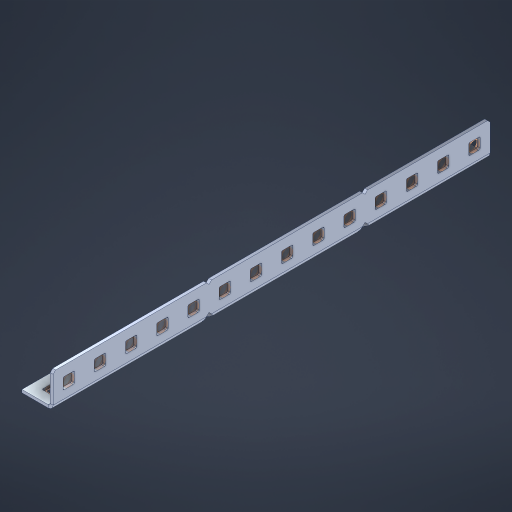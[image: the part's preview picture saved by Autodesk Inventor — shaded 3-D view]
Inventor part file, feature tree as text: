
AUTODESK INVENTOR PART (.ipt)
format: ipt  version: 2023 (Build 270158000, 158)  size: 627,712 bytes
history: native  units: in
note: dims shown in document units (in); Inventor stores cm internally (conversion verified against a paired STEP export)
features: other x33, extrude x27, sheet_metal_op x10, sketch x8, mirror x1, pattern_linear x1, chamfer x1
ambient origin geometry x8: Origin, YZ Plane, XZ Plane, XY Plane, X Axis, Y Axis, Z Axis, Center Point
bodies: Solid1 (feature_tree), Body (feature_tree)
feature tree (81):
  other  "Flange Pattern Plane"
  sheet_metal_op  "Flange Pattern"
  sheet_metal_op  "Body Pattern"
  other  "Arc Length"
  mirror  "Notch Mirror"
  pattern_linear  "Notch Pattern"  Spacing1=0.1875in  [1 undecoded]
  chamfer  "End Chamfer"
  extrude  "Half Cut"  Depth=0.0469in
  sketch  "Sketch1"  dims[d0=2.5in]
  other  "Plate1"
  sketch  "Sketch2"  dims[d1=7.0in]
  other  "Plate2"
  sheet_metal_op  "Bend1"
  sheet_metal_op  "Corner1"
  sketch  "Sketch3"  dims[d2=0.0469in]
  other  "Flange Pattern Sketch"
  sketch  "Sketch7"  dims[d3=0.0469in]
  other  "Srf1"
  other  "Srf2"
  sketch  "Sketch8"  dims[d4=0.0234in]
  sketch  "Sketch9"  dims[d5=0.0938in]
  other  "Srf91"
  sheet_metal_op  "Body Pattern Sketch"
  other  "Srf92"
  sketch  "Sketch13"  dims[d6=0.0469in]
  sketch  "Sketch14"  dims[d7=0.5in d8=90.0deg d9=0.0312in d10=0.1875in d11=0.0469in d12=0.0469in d16=0.182in d17=0.02in d18=0.0469in d19=0.0in d20=0.25in d21=0.25in d46=0.172in d47=1.0in d48=0.0in d49=0.182in d50=0.02in d51=0.25in d52=0.25in d53=0.0469in d54=0.0in d55=0.172in d56=1.0in d57=0.0in d60=5.5118in d62=0.5in d63=0.3937in d65=0.5in d85=0.1227in d86=0.1659in d88=0.04in d89=0.0469in d90=0.0in d91=0.04in d92=0.0491in d95=2.5in d96=0.04in d97=0.25in d98=45.0deg d101=0.0in d102=2.497in d131=0.5in d132=5.5118in d134=0.5in d139=0.5in]
  other  "Srf856"
  other  "Srf1310"
  other  "Srf1311"
  other  "Srf1312"
  other  "Srf1376"
  other  "Srf1377"
  other  "Srf1728"
  other  "Srf1755"
  other  "Srf1878"
  other  "Srf1879"
  other  "Srf1880"
  other  "Srf1881"
  other  "Srf1882"
  other  "Srf1883"
  other  "Srf1884"
  other  "Srf1885"
  other  "Srf1942"
  other  "Srf1943"
  other  "Srf1944"
  other  "Srf1945"
  other  "Srf1946"
  other  "Srf1947"
  other  "Srf1948"
  other  "Srf1949"
  sheet_metal_op  "Flange Stamp"
  sheet_metal_op  "Flange Circle"
  sheet_metal_op  "Body Stamp"
  sheet_metal_op  "Body Circle"
  sheet_metal_op  "Notch"
  extrude  "ExtrusionSrf2"  Depth=0.0469in
  extrude  "ExtrusionSrf92"  Depth=0.5in
  extrude  "ExtrusionSrf856"  Depth=0.02in
  extrude  "ExtrusionSrf1310"  Depth=0.0469in
  extrude  "ExtrusionSrf1311"  TaperAngle=0.0deg  [1 undecoded]
  extrude  "ExtrusionSrf1312"  Depth=0.5in
  extrude  "ExtrusionSrf1376"  Depth=0.5in
  extrude  "ExtrusionSrf1377"  Depth=0.5in
  extrude  "ExtrusionSrf1728"  Depth=0.5in TaperAngle=0.0deg
  extrude  "ExtrusionSrf1755"  Depth=0.5in
  extrude  "ExtrusionSrf1878"  Depth=0.02in
  extrude  "ExtrusionSrf1879"  Depth=0.5in
  extrude  "ExtrusionSrf1880"  Depth=0.5in
  extrude  "ExtrusionSrf1881"  Depth=0.0469in
  extrude  "ExtrusionSrf1882"  TaperAngle=0.0deg  [1 undecoded]
  extrude  "ExtrusionSrf1883"  Depth=0.5in
  extrude  "ExtrusionSrf1884"  Depth=0.5in TaperAngle=0.0deg
  extrude  "ExtrusionSrf1885"  Depth=0.5in
  extrude  "ExtrusionSrf1942"  Depth=0.5in
  extrude  "ExtrusionSrf1943"  Depth=0.5in
  extrude  "ExtrusionSrf1944"  Depth=0.5in
  extrude  "ExtrusionSrf1945"  Depth=0.5in
  extrude  "ExtrusionSrf1946"  Depth=0.0469in
  extrude  "ExtrusionSrf1947"  TaperAngle=0.0deg  [1 undecoded]
  extrude  "ExtrusionSrf1948"  Depth=0.5in
  extrude  "ExtrusionSrf1949"  Depth=0.5in
note: 4 required parameter values undecoded (feature->parameter linkage not recoverable at this tier; creation-order binding heuristic only, values carry confidence <= 0.55)
